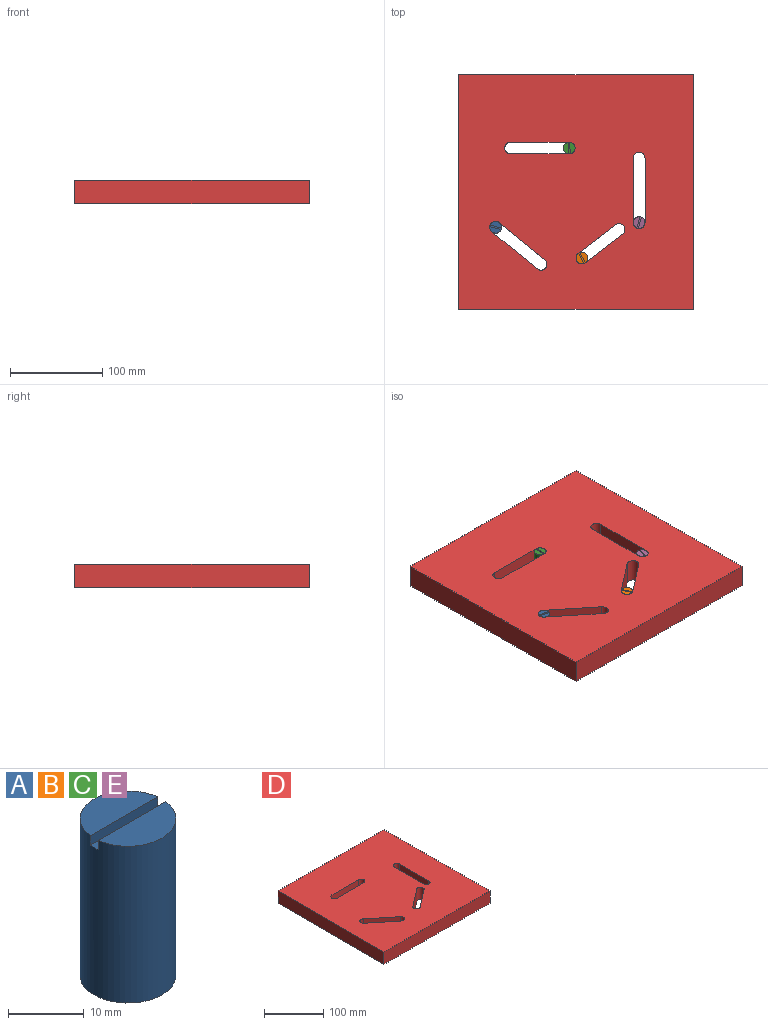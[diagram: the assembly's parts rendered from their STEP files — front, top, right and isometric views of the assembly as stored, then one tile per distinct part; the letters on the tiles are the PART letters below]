
ASSEMBLY  parts=5 mates=4
PART A: 7 faces, bbox 12.7x12.7x25.4 mm
  f0: plane 12.61x5.59mm, normal (0,0,1), area 53.7mm2, adj f1,f6
  f1: cylinder r=6.35mm len=25.4mm, axis (0,0,-1), area 1008.8mm2, adj f0,f2,f3,f4,f5,f6
  f2: plane 12.61x5.59mm, normal (0,0,1), area 53.7mm2, adj f1,f5
  f3: plane 12.7x12.7mm, normal (0,0,-1), area 126.7mm2, adj f1
  f4: plane 12.7x1.52mm, normal (0,0,1), area 19.3mm2, adj f1,f5,f6
  f5: plane 12.61x1.52mm, normal (0,1,0), area 19.2mm2, adj f1,f2,f4
  f6: plane 12.61x1.52mm, normal (0,-1,0), area 19.2mm2, adj f0,f1,f4
PART B: same geometry as A
PART C: same geometry as A
PART D: 22 faces, bbox 254x254x25.4 mm
  f0: plane 40.31x30.91mm, normal (0.61,-0.79,0), area 1290.3mm2, adj f1,f19,f20,f21
  f1: cylinder r=6.35mm len=25.4mm, axis (0,0,-1), area 506.7mm2, adj f0,f2,f20,f21
  f2: plane 40.31x30.91mm, normal (-0.61,0.79,0), area 1290.3mm2, adj f1,f19,f20,f21
  f3: plane 49.31x40.01mm, normal (-0.63,-0.78,0), area 1612.9mm2, adj f4,f15,f20,f21
  f4: cylinder r=6.35mm len=25.4mm, axis (0,0,-1), area 506.7mm2, adj f3,f5,f20,f21
  f5: plane 49.31x40.01mm, normal (0.63,0.78,0), area 1612.9mm2, adj f4,f15,f20,f21
  f6: plane 254x25.4mm, normal (1,0,0), area 6451.6mm2, adj f7,f16,f20,f21
  f7: plane 254x25.4mm, normal (0,1,0), area 6451.6mm2, adj f6,f8,f20,f21
  f8: plane 254x25.4mm, normal (-1,0,0), area 6451.6mm2, adj f7,f16,f20,f21
  f9: plane 63.5x25.4mm, normal (0,-1,0), area 1612.9mm2, adj f10,f17,f20,f21
  f10: cylinder r=6.35mm len=25.4mm, axis (0,0,-1), area 506.7mm2, adj f9,f11,f20,f21
  f11: plane 63.5x25.4mm, normal (0,1,0), area 1612.9mm2, adj f10,f17,f20,f21
  f12: plane 69.85x25.4mm, normal (-1,0,0), area 1774.2mm2, adj f13,f18,f20,f21
  f13: cylinder r=6.35mm len=25.4mm, axis (0,0,-1), area 506.7mm2, adj f12,f14,f20,f21
  f14: plane 69.85x25.4mm, normal (1,0,0), area 1774.2mm2, adj f13,f18,f20,f21
  f15: cylinder r=6.35mm len=25.4mm, axis (0,0,-1), area 506.7mm2, adj f3,f5,f20,f21
  f16: plane 254x25.4mm, normal (0,-1,0), area 6451.6mm2, adj f6,f8,f20,f21
  f17: cylinder r=6.35mm len=25.4mm, axis (0,0,-1), area 506.7mm2, adj f9,f11,f20,f21
  f18: cylinder r=6.35mm len=25.4mm, axis (0,0,-1), area 506.7mm2, adj f12,f14,f20,f21
  f19: cylinder r=6.35mm len=25.4mm, axis (0,0,-1), area 506.7mm2, adj f0,f2,f20,f21
  f20: plane 254x254mm, normal (0,0,1), area 60864.1mm2, adj f0,f1,f2,f3,f4,f5,f6,f7
  f21: plane 254x254mm, normal (0,0,-1), area 60864.1mm2, adj f0,f1,f2,f3,f4,f5,f6,f7
PART E: same geometry as A
PLACE A rot(axis=(0,0,-1),14.4deg) t=(85.2,-82.32,0)mm
PLACE B rot(axis=(0,0,-1),63.2deg) t=(86.47,-230.24,0)mm
PLACE C rot(axis=(0,0,-1),87.7deg) t=(-0.2,-130.17,0)mm
PLACE D at identity fixed
PLACE E rot(axis=(0,0,-1),106.3deg) t=(18.28,-203.77,0)mm
MATE pin_slot C.f1 <-> D.f17  axis (0,0,1) through (-7.31,47.49,25.4)mm
MATE pin_slot B.f1 <-> D.f19  axis (0,0,-1) through (6.35,-71.52,0)mm
MATE pin_slot E.f1 <-> D.f18  axis (0,0,1) through (68.31,-33.15,25.4)mm
MATE pin_slot A.f1 <-> D.f15  axis (0,0,-1) through (-87.04,-38.22,0)mm
